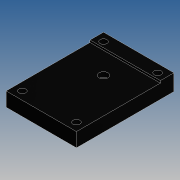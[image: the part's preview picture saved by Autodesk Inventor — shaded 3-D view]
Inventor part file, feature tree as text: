
AUTODESK INVENTOR PART (.ipt)
format: ipt  version: 2019 (Build 230136000, 136)  size: 235,008 bytes
history: native  units: mm
features: sketch x4, extrude x2, hole x2, pattern_linear x1, projected_geometry x1
ambient origin geometry x8: Origin, YZ Plane, XZ Plane, XY Plane, X Axis, Y Axis, Z Axis, Center Point
bodies: Solid1 (feature_tree)
feature tree (10):
  extrude  "Extrusion1"  Depth=15.0mm TaperAngle=0.0deg
  hole  "Hole1"  [1 undecoded]
  hole  "Hole2"  [1 undecoded]
  pattern_linear  "Rectangular Pattern2"  Spacing1=57.5mm  [1 undecoded]
  extrude  "Extrusion2"  Depth=2.0mm
  sketch  "Sketch1"  dims[d0=65.0mm d3=15.0mm d4=0.0mm]
  sketch  "Sketch2"  dims[d8=8.2mm d9=6.0mm d10=15.0mm d11=8.5mm d12=90.0deg d13=8.0mm d14=20.594885mm d16=25.0mm]
  sketch  "Sketch3"  dims[d17=25.0mm]
  sketch  "Sketch4"  dims[d18=6.3mm d19=6.0mm d20=11.0mm d21=7.0mm d22=90.0deg d23=8.0mm d24=20.594885mm d28=32.5mm d29=57.5mm d36=20.0mm d38=50.0mm d39=20.0mm d41=75.0mm d42=20.0mm d43=2.0mm d44=0.0mm]
  projected_geometry  "Project Cut Edges1"
note: 3 required parameter values undecoded (feature->parameter linkage not recoverable at this tier; creation-order binding heuristic only, values carry confidence <= 0.55)
